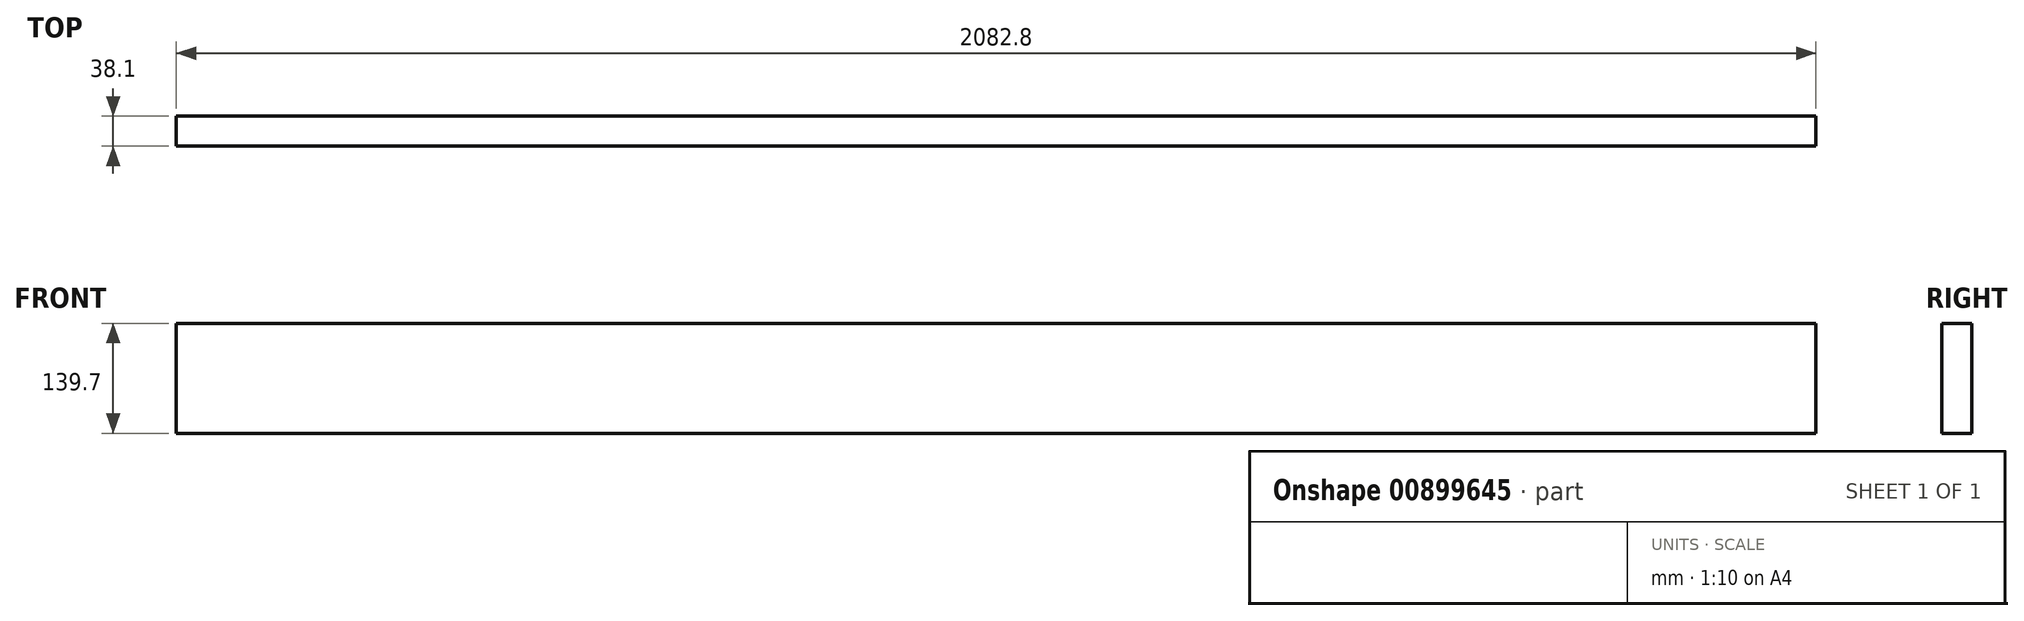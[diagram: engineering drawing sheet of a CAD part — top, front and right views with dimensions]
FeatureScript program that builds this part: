
annotation { "Feature Type Name" : "Feature", "Feature Type Description" : "" }
export const myFeature = defineFeature(function(context is Context, id is Id, definition is map)
    precondition{}
    {
        {
            var Q0;
            Q0=qCreatedBy(makeId("Front.planeOp"),FACE);
            var sketch = newSketch(context, id + "F0", { "sketchPlane" : qUnion([Q0])});
            skLineSegment(sketch, "E0.bottom", {"start": v(0, 0) * mm, "end": v(2082.8, 0) * mm});
            skLineSegment(sketch, "E0.top", {"start": v(0, 139.7) * mm, "end": v(2082.8, 139.7) * mm});
            skLineSegment(sketch, "E0.left", {"start": v(0, 0) * mm, "end": v(0, 139.7) * mm});
            skLineSegment(sketch, "E0.right", {"start": v(2082.8, 0) * mm, "end": v(2082.8, 139.7) * mm});
            skSolve(sketch);
        }
        {
            var Q0;
            Q0=makeQuery(id+"F0.imprint","IMPRINT",FACE,{"disambiguationData":[TD([[makeQuery(id+"F0.imprint","IMPRINT",EDGE,{"derivedFrom":sQuery(id+"F0.wireOp",EDGE,"E0.bottom")}),1.0]])]});
            extrude(context, id + "F1", {"entities" : qUnion([Q0]), "oppositeDirection" : true, "depth" : 38.1 * mm, "offsetDistance" : 25.4 * mm});
        }
    });
